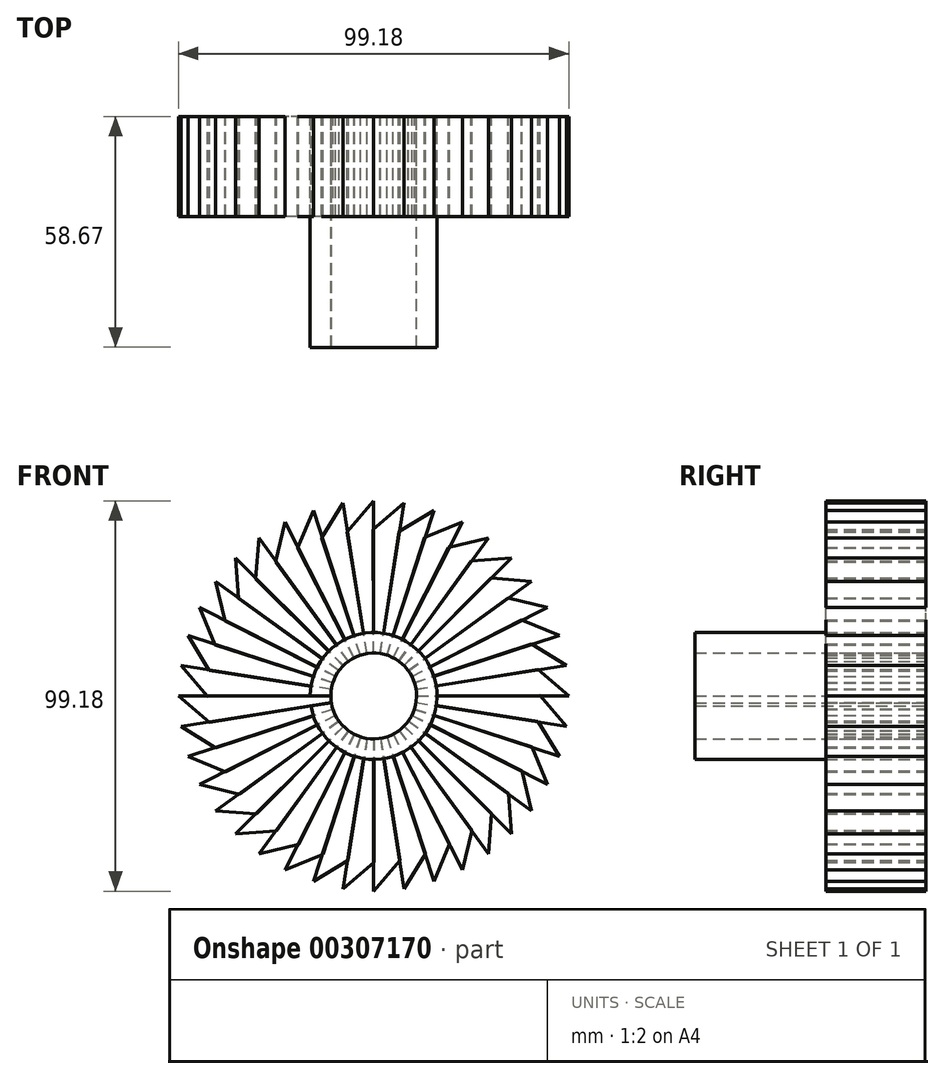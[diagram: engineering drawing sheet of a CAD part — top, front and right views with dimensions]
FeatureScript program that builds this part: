
annotation { "Feature Type Name" : "Feature", "Feature Type Description" : "" }
export const myFeature = defineFeature(function(context is Context, id is Id, definition is map)
    precondition{}
    {
        {
            var Q0;
            Q0=qCreatedBy(makeId("Front.planeOp"),FACE);
            var sketch = newSketch(context, id + "F0", { "sketchPlane" : qUnion([Q0])});
            skCircle(sketch, "E0", {"center": v(0, 0) * mm, "radius": 16.11 * mm});
            skCircle(sketch, "E1", {"center": v(0, 0) * mm, "radius": 10.89 * mm});
            skCircle(sketch, "E2", {"center": v(0, 0) * mm, "radius": 42.26 * mm, "construction": true});
            skCircle(sketch, "E3", {"center": v(0, 0) * mm, "radius": 49.6 * mm, "construction": true});
            skLineSegment(sketch, "E4", {"start": v(0, 0) * mm, "end": v(-48.95, -7.93) * mm});
            skLineSegment(sketch, "E5", {"start": v(-41.72, -6.75) * mm, "end": v(-49.6, 0) * mm});
            skLineSegment(sketch, "E6", {"start": v(0, 0) * mm, "end": v(-49.6, 0) * mm});
            skSolve(sketch);
        }
        {
            var Q0;
            {var subQ5=sQuery(id+"F0.wireOp",EDGE,"E5");Q0=makeQuery(id+"F0.imprint","IMPRINT",FACE,{"disambiguationData":[TD([[makeQuery(id+"F0.imprint","IMPRINT",EDGE,{"derivedFrom":subQ5}),-1.0]])]});}
            var Q1;
            {var subQ0=sQuery(id+"F0.wireOp",EDGE,"E4");var subQ1=sQuery(id+"F0.wireOp",EDGE,"E0");var subQ2=makeQuery(id+"F0.imprint","INTERSECT",VERTEX,{"derivedFrom":[subQ1,subQ0]});Q1=makeQuery(id+"F0.imprint","IMPRINT",FACE,{"disambiguationData":[TD([[makeQuery(id+"F0.imprint","IMPRINT",EDGE,{"disambiguationData":[TD([[subQ2,1.0]])],"derivedFrom":subQ1}),1.0]])]});}
            extrude(context, id + "F1", {"entities" : qUnion([Q0, Q1]), "depth" : 25.4 * mm});
        }
        {
            var Q0;
            Q0=makeQuery(id+"F1.opExtrude","SWEPT_BODY",BODY,{"disambiguationData":[OSD([sQuery(id+"F0.wireOp",EDGE,"E1"),sQuery(id+"F0.wireOp",EDGE,"E4"),sQuery(id+"F0.wireOp",EDGE,"E5"),sQuery(id+"F0.wireOp",EDGE,"E6")])]});
            var Q1;
            Q1=sQuery(id+"F0.wireOp",EDGE,"E1");
            circularPattern(context, id + "F2", {"entities" : qUnion([Q0]), "axis" : qUnion([Q1]), "angle" : 360 * degree, "instanceCount" : 40, "equalSpace" : true});
        }
        {
            var Q0;
            {var subQ0=sQuery(id+"F0.wireOp",EDGE,"E4");var subQ1=sQuery(id+"F0.wireOp",EDGE,"E0");var subQ2=makeQuery(id+"F0.imprint","INTERSECT",VERTEX,{"derivedFrom":[subQ1,subQ0]});Q0=makeQuery(id+"F0.imprint","IMPRINT",FACE,{"disambiguationData":[TD([[makeQuery(id+"F0.imprint","IMPRINT",EDGE,{"disambiguationData":[TD([[subQ2,-1.0]])],"derivedFrom":subQ1}),1.0]])]});}
            extrude(context, id + "F3", {"entities" : qUnion([Q0]), "depth" : 58.67 * mm});
        }
    });
